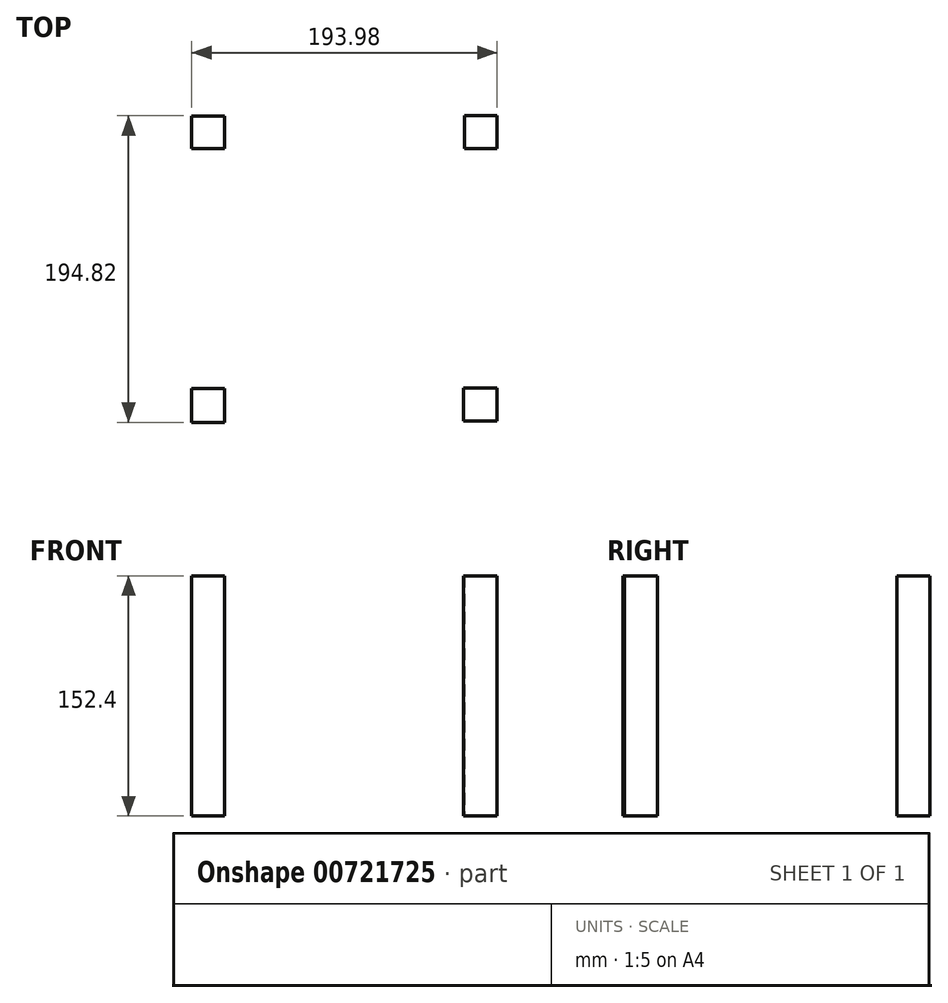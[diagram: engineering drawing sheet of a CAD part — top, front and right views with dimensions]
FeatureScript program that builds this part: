
annotation { "Feature Type Name" : "Feature", "Feature Type Description" : "" }
export const myFeature = defineFeature(function(context is Context, id is Id, definition is map)
    precondition{}
    {
        {
            var Q0;
            Q0=qCreatedBy(makeId("Top.planeOp"),FACE);
            var sketch = newSketch(context, id + "F0", { "sketchPlane" : qUnion([Q0])});
            skLineSegment(sketch, "E0.bottom", {"start": v(-96.94, 96.87) * mm, "end": v(-76.1, 96.87) * mm});
            skLineSegment(sketch, "E0.top", {"start": v(-96.94, 76.17) * mm, "end": v(-76.1, 76.17) * mm});
            skLineSegment(sketch, "E0.left", {"start": v(-96.94, 96.87) * mm, "end": v(-96.94, 76.17) * mm});
            skLineSegment(sketch, "E0.right", {"start": v(-76.1, 96.87) * mm, "end": v(-76.1, 76.17) * mm});
            skLineSegment(sketch, "E1.bottom", {"start": v(-76.2, -76.14) * mm, "end": v(-96.87, -76.14) * mm});
            skLineSegment(sketch, "E1.top", {"start": v(-76.2, -97.82) * mm, "end": v(-96.87, -97.82) * mm});
            skLineSegment(sketch, "E1.left", {"start": v(-76.2, -76.14) * mm, "end": v(-76.2, -97.82) * mm});
            skLineSegment(sketch, "E1.right", {"start": v(-96.87, -76.14) * mm, "end": v(-96.87, -97.82) * mm});
            skLineSegment(sketch, "E2.bottom", {"start": v(96.94, -96.99) * mm, "end": v(75.84, -96.99) * mm});
            skLineSegment(sketch, "E2.top", {"start": v(96.94, -76.07) * mm, "end": v(75.84, -76.07) * mm});
            skLineSegment(sketch, "E2.left", {"start": v(96.94, -96.99) * mm, "end": v(96.94, -76.07) * mm});
            skLineSegment(sketch, "E2.right", {"start": v(75.84, -96.99) * mm, "end": v(75.84, -76.07) * mm});
            skLineSegment(sketch, "E3.bottom", {"start": v(76.28, 76.23) * mm, "end": v(97.04, 76.23) * mm});
            skLineSegment(sketch, "E3.top", {"start": v(76.28, 97) * mm, "end": v(97.04, 97) * mm});
            skLineSegment(sketch, "E3.left", {"start": v(76.28, 76.23) * mm, "end": v(76.28, 97) * mm});
            skLineSegment(sketch, "E3.right", {"start": v(97.04, 76.23) * mm, "end": v(97.04, 97) * mm});
            skSolve(sketch);
        }
        {
            var Q0;
            Q0=makeQuery(id+"F0.imprint","IMPRINT",FACE,{"disambiguationData":[TD([[makeQuery(id+"F0.imprint","IMPRINT",EDGE,{"derivedFrom":sQuery(id+"F0.wireOp",EDGE,"E0.bottom")}),-1.0]])]});
            var Q1;
            Q1=makeQuery(id+"F0.imprint","IMPRINT",FACE,{"disambiguationData":[TD([[makeQuery(id+"F0.imprint","IMPRINT",EDGE,{"derivedFrom":sQuery(id+"F0.wireOp",EDGE,"E2.bottom")}),-1.0]])]});
            var Q2;
            Q2=makeQuery(id+"F0.imprint","IMPRINT",FACE,{"disambiguationData":[TD([[makeQuery(id+"F0.imprint","IMPRINT",EDGE,{"derivedFrom":sQuery(id+"F0.wireOp",EDGE,"E0.bottom")}),-1.0]])]});
            var Q3;
            Q3=makeQuery(id+"F0.imprint","IMPRINT",FACE,{"disambiguationData":[TD([[makeQuery(id+"F0.imprint","IMPRINT",EDGE,{"derivedFrom":sQuery(id+"F0.wireOp",EDGE,"E1.bottom")}),1.0]])]});
            var Q4;
            Q4=makeQuery(id+"F0.imprint","IMPRINT",FACE,{"disambiguationData":[TD([[makeQuery(id+"F0.imprint","IMPRINT",EDGE,{"derivedFrom":sQuery(id+"F0.wireOp",EDGE,"E3.bottom")}),1.0]])]});
            extrude(context, id + "F1", {"entities" : qUnion([Q0, Q1, Q2, Q3, Q4]), "depth" : 127 * mm, "offsetDistance" : 25.4 * mm, "hasSecondDirection" : true, "secondDirectionOppositeDirection" : true, "secondDirectionDepth" : 25.4 * mm});
        }
    });
